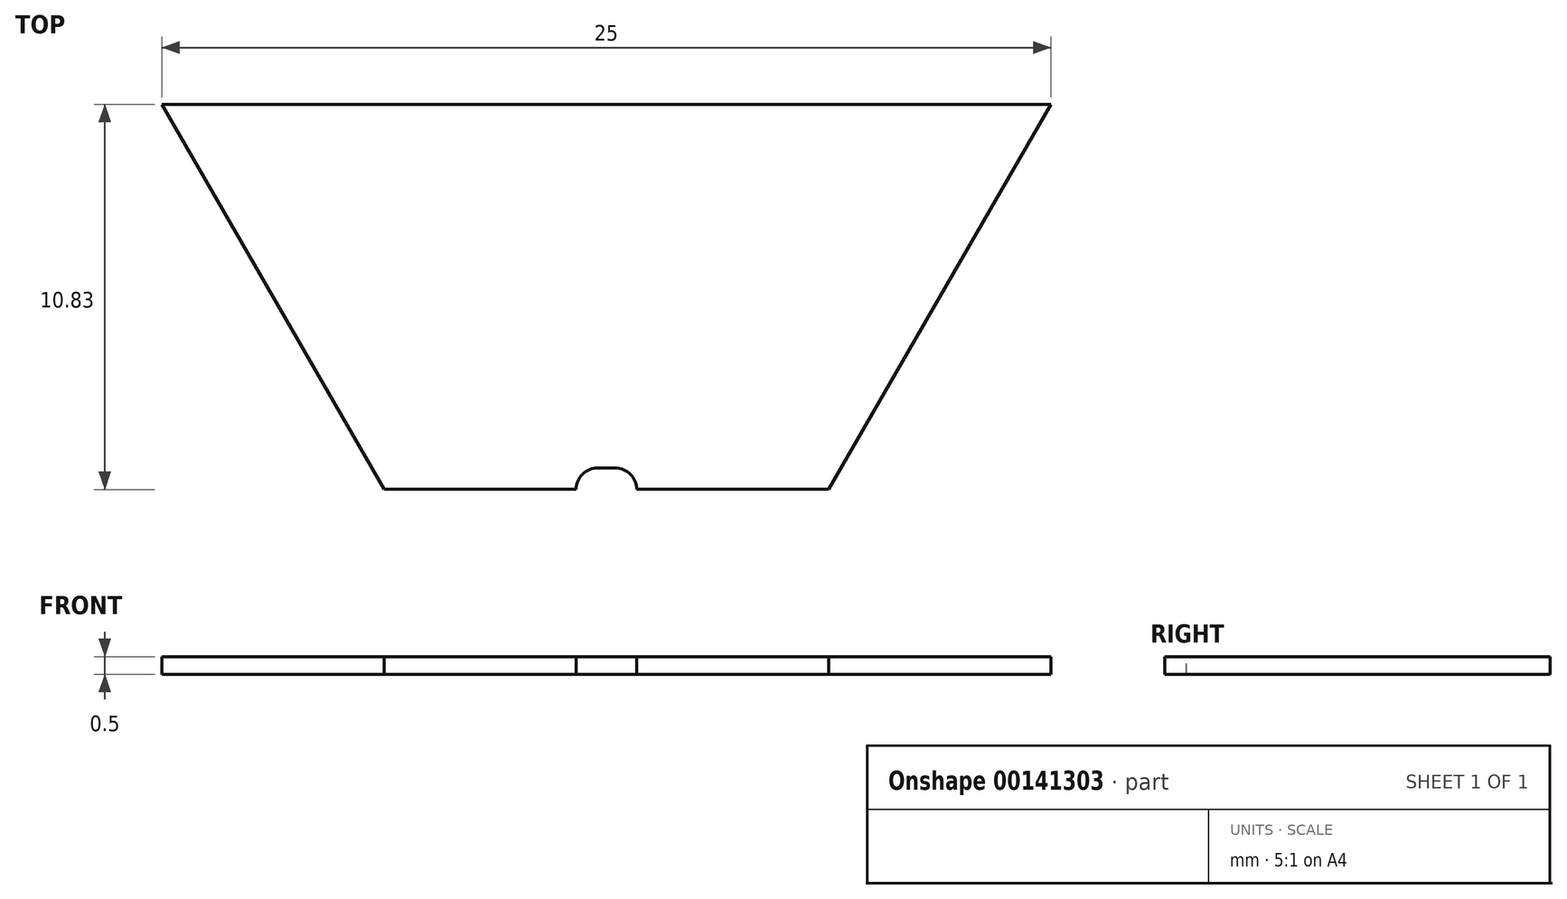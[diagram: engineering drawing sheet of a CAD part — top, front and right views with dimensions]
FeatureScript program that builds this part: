
annotation { "Feature Type Name" : "Feature", "Feature Type Description" : "" }
export const myFeature = defineFeature(function(context is Context, id is Id, definition is map)
    precondition{}
    {
        {
            var Q0;
            Q0=qCreatedBy(makeId("Top.planeOp"),FACE);
            var sketch = newSketch(context, id + "F0", { "sketchPlane" : qUnion([Q0])});
            skCircle(sketch, "E0.cCircle", {"center": v(0, 0) * mm, "radius": 12.5 * mm, "construction": true});
            skLineSegment(sketch, "E0.0", {"start": v(12.5, 0) * mm, "end": v(6.25, -10.83) * mm});
            skLineSegment(sketch, "E0.1", {"start": v(6.25, -10.83) * mm, "end": v(-6.25, -10.83) * mm});
            skLineSegment(sketch, "E0.2", {"start": v(-6.25, -10.83) * mm, "end": v(-12.5, 0) * mm});
            skLineSegment(sketch, "E0.3", {"start": v(-12.5, 0) * mm, "end": v(-6.25, 10.83) * mm});
            skLineSegment(sketch, "E0.4", {"start": v(-6.25, 10.83) * mm, "end": v(6.25, 10.83) * mm});
            skLineSegment(sketch, "E0.5", {"start": v(6.25, 10.83) * mm, "end": v(12.5, 0) * mm});
            skSolve(sketch);
        }
        {
            var Q0;
            Q0=qSketchRegion(id+"F0",true);
            extrude(context, id + "F1", {"entities" : qUnion([Q0]), "depth" : 0.5 * mm});
        }
        {
            var Q0;
            Q0=makeQuery(id+"F1.opExtrude","CAP_FACE",FACE,{"disambiguationData":[OSD([sQuery(id+"F0.wireOp",EDGE,"E0.0"),sQuery(id+"F0.wireOp",EDGE,"E0.1"),sQuery(id+"F0.wireOp",EDGE,"E0.2"),sQuery(id+"F0.wireOp",EDGE,"E0.3"),sQuery(id+"F0.wireOp",EDGE,"E0.4"),sQuery(id+"F0.wireOp",EDGE,"E0.5")])],"isStart":false});
            var sketch = newSketch(context, id + "F2", { "sketchPlane" : qUnion([Q0])});
            skLineSegment(sketch, "E1.0", {"start": v(6.25, -10.83) * mm, "end": v(-6.25, -10.83) * mm, "construction": true});
            skLineSegment(sketch, "E2", {"start": v(0.25, -10.23) * mm, "end": v(-0.25, -10.23) * mm});
            skArc(sketch, "E3", {"start": v(-0.25, -10.23) * mm, "mid": v(-0.67, -10.4) * mm, "end": v(-0.85, -10.83) * mm});
            skArc(sketch, "E4", {"start": v(0.85, -10.83) * mm, "mid": v(0.67, -10.4) * mm, "end": v(0.25, -10.23) * mm});
            skLineSegment(sketch, "E5", {"start": v(-0.85, -10.83) * mm, "end": v(0.85, -10.83) * mm});
            skSolve(sketch);
        }
        {
            var Q0;
            Q0=makeQuery(id+"F2.imprint","IMPRINT",FACE,{"disambiguationData":[TD([[makeQuery(id+"F2.imprint","IMPRINT",EDGE,{"derivedFrom":sQuery(id+"F2.wireOp",EDGE,"E2")}),1.0]])]});
            extrude(context, id + "F3", {"entities" : qUnion([Q0]), "operationType" : NewBodyOperationType.REMOVE, "endBound" : BoundingType.THROUGH_ALL, "oppositeDirection" : true, "depth" : 25 * mm});
        }
        {
            var Q0;
            Q0=makeQuery(id+"F1.opExtrude","CAP_FACE",FACE,{"disambiguationData":[OSD([sQuery(id+"F0.wireOp",EDGE,"E0.0"),sQuery(id+"F0.wireOp",EDGE,"E0.1"),sQuery(id+"F0.wireOp",EDGE,"E0.2"),sQuery(id+"F0.wireOp",EDGE,"E0.3"),sQuery(id+"F0.wireOp",EDGE,"E0.4"),sQuery(id+"F0.wireOp",EDGE,"E0.5")])],"isStart":false});
            var sketch = newSketch(context, id + "F4", { "sketchPlane" : qUnion([Q0])});
            skLineSegment(sketch, "E6", {"start": v(-12.5, 0) * mm, "end": v(12.5, 0) * mm});
            skLineSegment(sketch, "E7", {"start": v(12.5, 0) * mm, "end": v(6.25, 10.83) * mm});
            skLineSegment(sketch, "E8", {"start": v(6.25, 10.83) * mm, "end": v(-6.25, 10.83) * mm});
            skLineSegment(sketch, "E9", {"start": v(-6.25, 10.83) * mm, "end": v(-12.5, 0) * mm});
            skSolve(sketch);
        }
        {
            var Q0;
            Q0=makeQuery(id+"F4.imprint","IMPRINT",FACE,{"disambiguationData":[TD([[makeQuery(id+"F4.imprint","IMPRINT",EDGE,{"derivedFrom":sQuery(id+"F4.wireOp",EDGE,"E6")}),1.0]])]});
            extrude(context, id + "F5", {"entities" : qUnion([Q0]), "operationType" : NewBodyOperationType.REMOVE, "endBound" : BoundingType.THROUGH_ALL, "oppositeDirection" : true, "depth" : 25 * mm});
        }
    });
